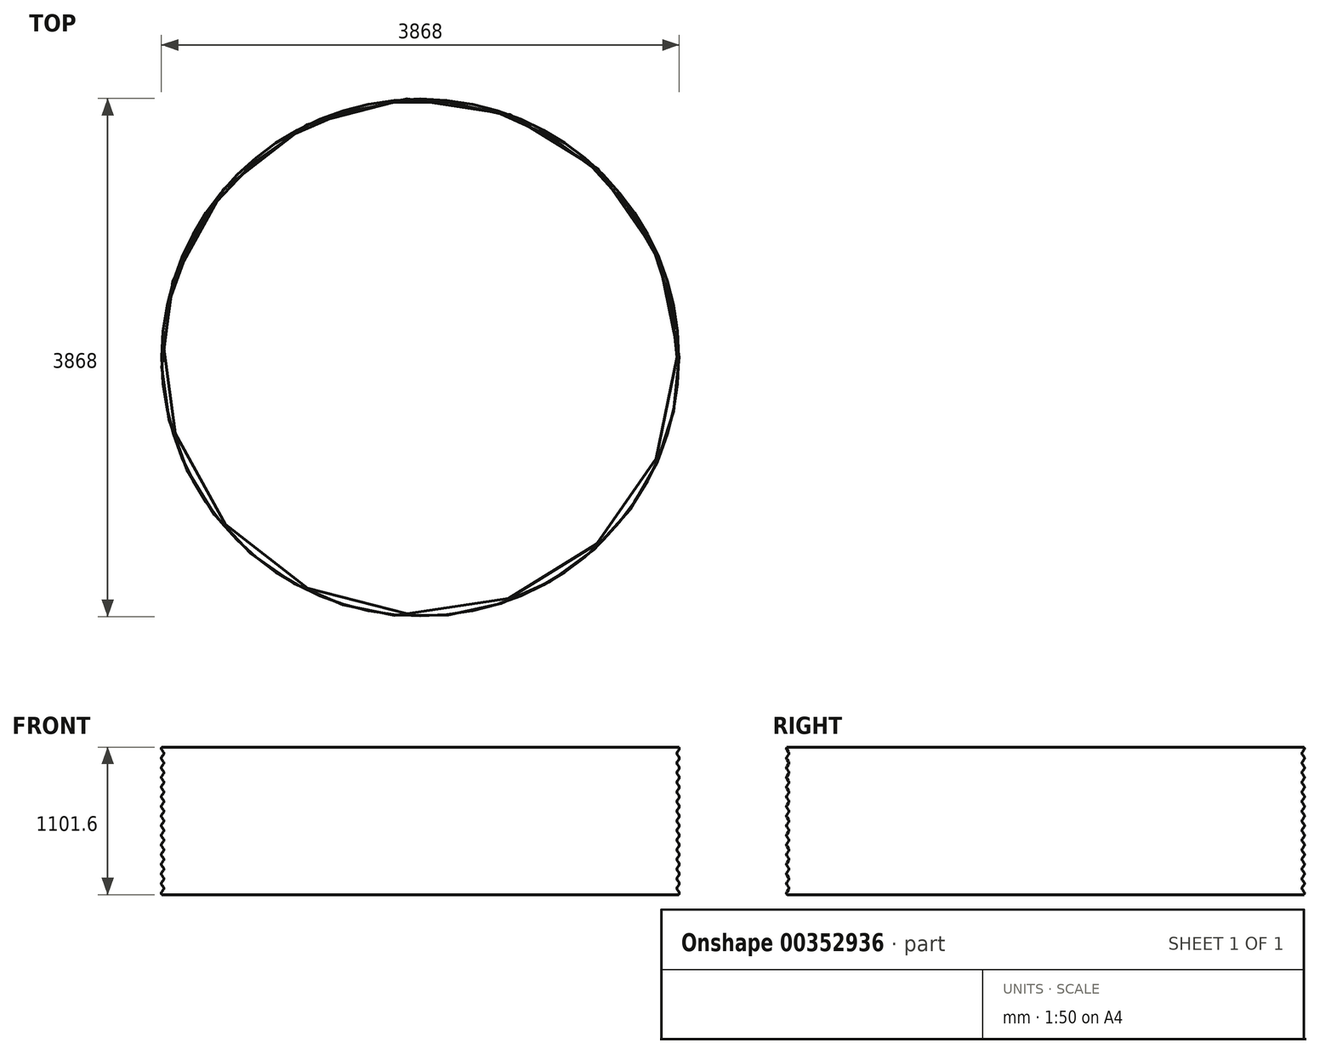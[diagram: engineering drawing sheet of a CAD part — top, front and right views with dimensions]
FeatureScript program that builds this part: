
annotation { "Feature Type Name" : "Feature", "Feature Type Description" : "" }
export const myFeature = defineFeature(function(context is Context, id is Id, definition is map)
    precondition{}
    {
        {
            var Q0;
            Q0=qCreatedBy(makeId("Front.planeOp"),FACE);
            var sketch = newSketch(context, id + "F0", { "sketchPlane" : qUnion([Q0])});
            skLineSegment(sketch, "E0", {"start": v(-1925, 0) * mm, "end": v(-1925, 72) * mm, "construction": true});
            skLineSegment(sketch, "E1", {"start": v(-1916, 0) * mm, "end": v(-1916, 72) * mm, "construction": true});
            skLineSegment(sketch, "E2", {"start": v(-1934, 0) * mm, "end": v(-1934, 72) * mm, "construction": true});
            skLineSegment(sketch, "E3", {"start": v(-1930.4, 10.8) * mm, "end": v(-1919.6, 25.2) * mm});
            skLineSegment(sketch, "E4", {"start": v(-1919.6, 46.8) * mm, "end": v(-1930.4, 61.2) * mm});
            skArc(sketch, "E5", {"start": v(-1930.4, -10.8) * mm, "mid": v(-1898, 0) * mm, "end": v(-1930.4, 10.8) * mm, "construction": true});
            skArc(sketch, "E6", {"start": v(-1930.4, 10.8) * mm, "mid": v(-1934, 0) * mm, "end": v(-1930.4, -10.8) * mm});
            skArc(sketch, "E7", {"start": v(-1919.6, 25.2) * mm, "mid": v(-1916, 36) * mm, "end": v(-1919.6, 46.8) * mm});
            skArc(sketch, "E8", {"start": v(-1919.6, 46.8) * mm, "mid": v(-1952, 36) * mm, "end": v(-1919.6, 25.2) * mm, "construction": true});
            skPoint(sketch, "E9", {"position": v(-1916, 36) * mm});
            skArc(sketch, "E10", {"start": v(-1930.4, 61.2) * mm, "mid": v(-1898, 72) * mm, "end": v(-1930.4, 82.8) * mm, "construction": true});
            skArc(sketch, "E11", {"start": v(-1930.4, 82.8) * mm, "mid": v(-1934, 72) * mm, "end": v(-1930.4, 61.2) * mm});
            skLineSegment(sketch, "E12", {"start": v(0, 0) * mm, "end": v(0, 1237.26) * mm, "construction": true});
            skLineSegment(sketch, "E13.0.1.0", {"start": v(-1930.4, 82.8) * mm, "end": v(-1919.6, 97.2) * mm});
            skArc(sketch, "E13.0.1.1", {"start": v(-1919.6, 97.2) * mm, "mid": v(-1916, 108) * mm, "end": v(-1919.6, 118.8) * mm});
            skLineSegment(sketch, "E13.0.1.2", {"start": v(-1919.6, 118.8) * mm, "end": v(-1930.4, 133.2) * mm});
            skArc(sketch, "E13.0.1.3", {"start": v(-1930.4, 154.8) * mm, "mid": v(-1934, 144) * mm, "end": v(-1930.4, 133.2) * mm});
            skLineSegment(sketch, "E13.0.2.0", {"start": v(-1930.4, 154.8) * mm, "end": v(-1919.6, 169.2) * mm});
            skArc(sketch, "E13.0.2.1", {"start": v(-1919.6, 169.2) * mm, "mid": v(-1916, 180) * mm, "end": v(-1919.6, 190.8) * mm});
            skLineSegment(sketch, "E13.0.2.2", {"start": v(-1919.6, 190.8) * mm, "end": v(-1930.4, 205.2) * mm});
            skArc(sketch, "E13.0.2.3", {"start": v(-1930.4, 226.8) * mm, "mid": v(-1934, 216) * mm, "end": v(-1930.4, 205.2) * mm});
            skLineSegment(sketch, "E13.0.3.0", {"start": v(-1930.4, 226.8) * mm, "end": v(-1919.6, 241.2) * mm});
            skArc(sketch, "E13.0.3.1", {"start": v(-1919.6, 241.2) * mm, "mid": v(-1916, 252) * mm, "end": v(-1919.6, 262.8) * mm});
            skLineSegment(sketch, "E13.0.3.2", {"start": v(-1919.6, 262.8) * mm, "end": v(-1930.4, 277.2) * mm});
            skArc(sketch, "E13.0.3.3", {"start": v(-1930.4, 298.8) * mm, "mid": v(-1934, 288) * mm, "end": v(-1930.4, 277.2) * mm});
            skLineSegment(sketch, "E13.0.4.0", {"start": v(-1930.4, 298.8) * mm, "end": v(-1919.6, 313.2) * mm});
            skArc(sketch, "E13.0.4.1", {"start": v(-1919.6, 313.2) * mm, "mid": v(-1916, 324) * mm, "end": v(-1919.6, 334.8) * mm});
            skLineSegment(sketch, "E13.0.4.2", {"start": v(-1919.6, 334.8) * mm, "end": v(-1930.4, 349.2) * mm});
            skArc(sketch, "E13.0.4.3", {"start": v(-1930.4, 370.8) * mm, "mid": v(-1934, 360) * mm, "end": v(-1930.4, 349.2) * mm});
            skLineSegment(sketch, "E13.0.5.0", {"start": v(-1930.4, 370.8) * mm, "end": v(-1919.6, 385.2) * mm});
            skArc(sketch, "E13.0.5.1", {"start": v(-1919.6, 385.2) * mm, "mid": v(-1916, 396) * mm, "end": v(-1919.6, 406.8) * mm});
            skLineSegment(sketch, "E13.0.5.2", {"start": v(-1919.6, 406.8) * mm, "end": v(-1930.4, 421.2) * mm});
            skArc(sketch, "E13.0.5.3", {"start": v(-1930.4, 442.8) * mm, "mid": v(-1934, 432) * mm, "end": v(-1930.4, 421.2) * mm});
            skLineSegment(sketch, "E13.0.6.0", {"start": v(-1930.4, 442.8) * mm, "end": v(-1919.6, 457.2) * mm});
            skArc(sketch, "E13.0.6.1", {"start": v(-1919.6, 457.2) * mm, "mid": v(-1916, 468) * mm, "end": v(-1919.6, 478.8) * mm});
            skLineSegment(sketch, "E13.0.6.2", {"start": v(-1919.6, 478.8) * mm, "end": v(-1930.4, 493.2) * mm});
            skArc(sketch, "E13.0.6.3", {"start": v(-1930.4, 514.8) * mm, "mid": v(-1934, 504) * mm, "end": v(-1930.4, 493.2) * mm});
            skLineSegment(sketch, "E13.0.7.0", {"start": v(-1930.4, 514.8) * mm, "end": v(-1919.6, 529.2) * mm});
            skArc(sketch, "E13.0.7.1", {"start": v(-1919.6, 529.2) * mm, "mid": v(-1916, 540) * mm, "end": v(-1919.6, 550.8) * mm});
            skLineSegment(sketch, "E13.0.7.2", {"start": v(-1919.6, 550.8) * mm, "end": v(-1930.4, 565.2) * mm});
            skArc(sketch, "E13.0.7.3", {"start": v(-1930.4, 586.8) * mm, "mid": v(-1934, 576) * mm, "end": v(-1930.4, 565.2) * mm});
            skLineSegment(sketch, "E13.0.8.0", {"start": v(-1930.4, 586.8) * mm, "end": v(-1919.6, 601.2) * mm});
            skArc(sketch, "E13.0.8.1", {"start": v(-1919.6, 601.2) * mm, "mid": v(-1916, 612) * mm, "end": v(-1919.6, 622.8) * mm});
            skLineSegment(sketch, "E13.0.8.2", {"start": v(-1919.6, 622.8) * mm, "end": v(-1930.4, 637.2) * mm});
            skArc(sketch, "E13.0.8.3", {"start": v(-1930.4, 658.8) * mm, "mid": v(-1934, 648) * mm, "end": v(-1930.4, 637.2) * mm});
            skLineSegment(sketch, "E13.0.9.0", {"start": v(-1930.4, 658.8) * mm, "end": v(-1919.6, 673.2) * mm});
            skArc(sketch, "E13.0.9.1", {"start": v(-1919.6, 673.2) * mm, "mid": v(-1916, 684) * mm, "end": v(-1919.6, 694.8) * mm});
            skLineSegment(sketch, "E13.0.9.2", {"start": v(-1919.6, 694.8) * mm, "end": v(-1930.4, 709.2) * mm});
            skArc(sketch, "E13.0.9.3", {"start": v(-1930.4, 730.8) * mm, "mid": v(-1934, 720) * mm, "end": v(-1930.4, 709.2) * mm});
            skLineSegment(sketch, "E13.0.10.0", {"start": v(-1930.4, 730.8) * mm, "end": v(-1919.6, 745.2) * mm});
            skArc(sketch, "E13.0.10.1", {"start": v(-1919.6, 745.2) * mm, "mid": v(-1916, 756) * mm, "end": v(-1919.6, 766.8) * mm});
            skLineSegment(sketch, "E13.0.10.2", {"start": v(-1919.6, 766.8) * mm, "end": v(-1930.4, 781.2) * mm});
            skArc(sketch, "E13.0.10.3", {"start": v(-1930.4, 802.8) * mm, "mid": v(-1934, 792) * mm, "end": v(-1930.4, 781.2) * mm});
            skLineSegment(sketch, "E13.0.11.0", {"start": v(-1930.4, 802.8) * mm, "end": v(-1919.6, 817.2) * mm});
            skArc(sketch, "E13.0.11.1", {"start": v(-1919.6, 817.2) * mm, "mid": v(-1916, 828) * mm, "end": v(-1919.6, 838.8) * mm});
            skLineSegment(sketch, "E13.0.11.2", {"start": v(-1919.6, 838.8) * mm, "end": v(-1930.4, 853.2) * mm});
            skArc(sketch, "E13.0.11.3", {"start": v(-1930.4, 874.8) * mm, "mid": v(-1934, 864) * mm, "end": v(-1930.4, 853.2) * mm});
            skLineSegment(sketch, "E13.0.12.0", {"start": v(-1930.4, 874.8) * mm, "end": v(-1919.6, 889.2) * mm});
            skArc(sketch, "E13.0.12.1", {"start": v(-1919.6, 889.2) * mm, "mid": v(-1916, 900) * mm, "end": v(-1919.6, 910.8) * mm});
            skLineSegment(sketch, "E13.0.12.2", {"start": v(-1919.6, 910.8) * mm, "end": v(-1930.4, 925.2) * mm});
            skArc(sketch, "E13.0.12.3", {"start": v(-1930.4, 946.8) * mm, "mid": v(-1934, 936) * mm, "end": v(-1930.4, 925.2) * mm});
            skLineSegment(sketch, "E13.0.13.0", {"start": v(-1930.4, 946.8) * mm, "end": v(-1919.6, 961.2) * mm});
            skArc(sketch, "E13.0.13.1", {"start": v(-1919.6, 961.2) * mm, "mid": v(-1916, 972) * mm, "end": v(-1919.6, 982.8) * mm});
            skLineSegment(sketch, "E13.0.13.2", {"start": v(-1919.6, 982.8) * mm, "end": v(-1930.4, 997.2) * mm});
            skArc(sketch, "E13.0.13.3", {"start": v(-1930.4, 1018.8) * mm, "mid": v(-1934, 1008) * mm, "end": v(-1930.4, 997.2) * mm});
            skLineSegment(sketch, "E13.0.14.0", {"start": v(-1930.4, 1018.8) * mm, "end": v(-1919.6, 1033.2) * mm});
            skArc(sketch, "E13.0.14.1", {"start": v(-1919.6, 1033.2) * mm, "mid": v(-1916, 1044) * mm, "end": v(-1919.6, 1054.8) * mm});
            skLineSegment(sketch, "E13.0.14.2", {"start": v(-1919.6, 1054.8) * mm, "end": v(-1930.4, 1069.2) * mm});
            skArc(sketch, "E13.0.14.3", {"start": v(-1930.4, 1090.8) * mm, "mid": v(-1934, 1080) * mm, "end": v(-1930.4, 1069.2) * mm});
            skLineSegment(sketch, "E13.direction1", {"start": v(-1930.4, 10.8) * mm, "end": v(-1870, 10.8) * mm, "construction": true});
            skLineSegment(sketch, "E13.direction2", {"start": v(-1930.4, 10.8) * mm, "end": v(-1930.4, 82.8) * mm, "construction": true});
            skSolve(sketch);
        }
        {
            var Q0;
            Q0=qConstructionFilter(qBodyType(qCreatedBy(id+"F0",EDGE),BodyType.WIRE),ConstructionObject.NO);
            var Q1;
            Q1=sQuery(id+"F0.wireOp",EDGE,"E12");
            revolve(context, id + "F1", {"bodyType" : ToolBodyType.SURFACE, "surfaceEntities" : qUnion([Q0]), "axis" : qUnion([Q1]), "revolveType" : RevolveType.FULL});
        }
    });
